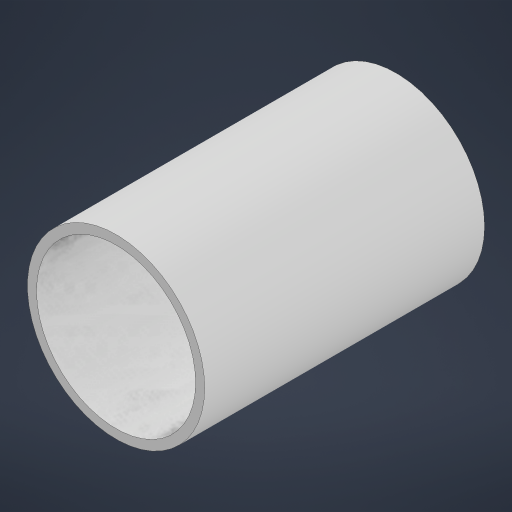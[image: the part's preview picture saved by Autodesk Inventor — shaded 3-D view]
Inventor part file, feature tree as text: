
AUTODESK INVENTOR PART (.ipt)
format: ipt  version: 2024 (Build 280153000, 153)  size: 181,248 bytes
history: native  units: mm
features: extrude x2, sketch x2, other x1
ambient origin geometry x8: Origin, YZ Plane, XZ Plane, XY Plane, X Axis, Y Axis, Z Axis, Center Point
bodies: Body1 (feature_tree)
feature tree (5):
  other  "Sólido1"
  extrude  "Extrusión1"  Depth=300.0mm TaperAngle=0.0deg
  extrude  "Extrusión3"  Depth=3000.0mm TaperAngle=0.0deg
  sketch  "Boceto1"  dims[d0=190.0mm d1=300.0mm d2=0.0mm]
  sketch  "Boceto3"  dims[d6=170.62mm d7=3000.0mm d8=0.0mm]
